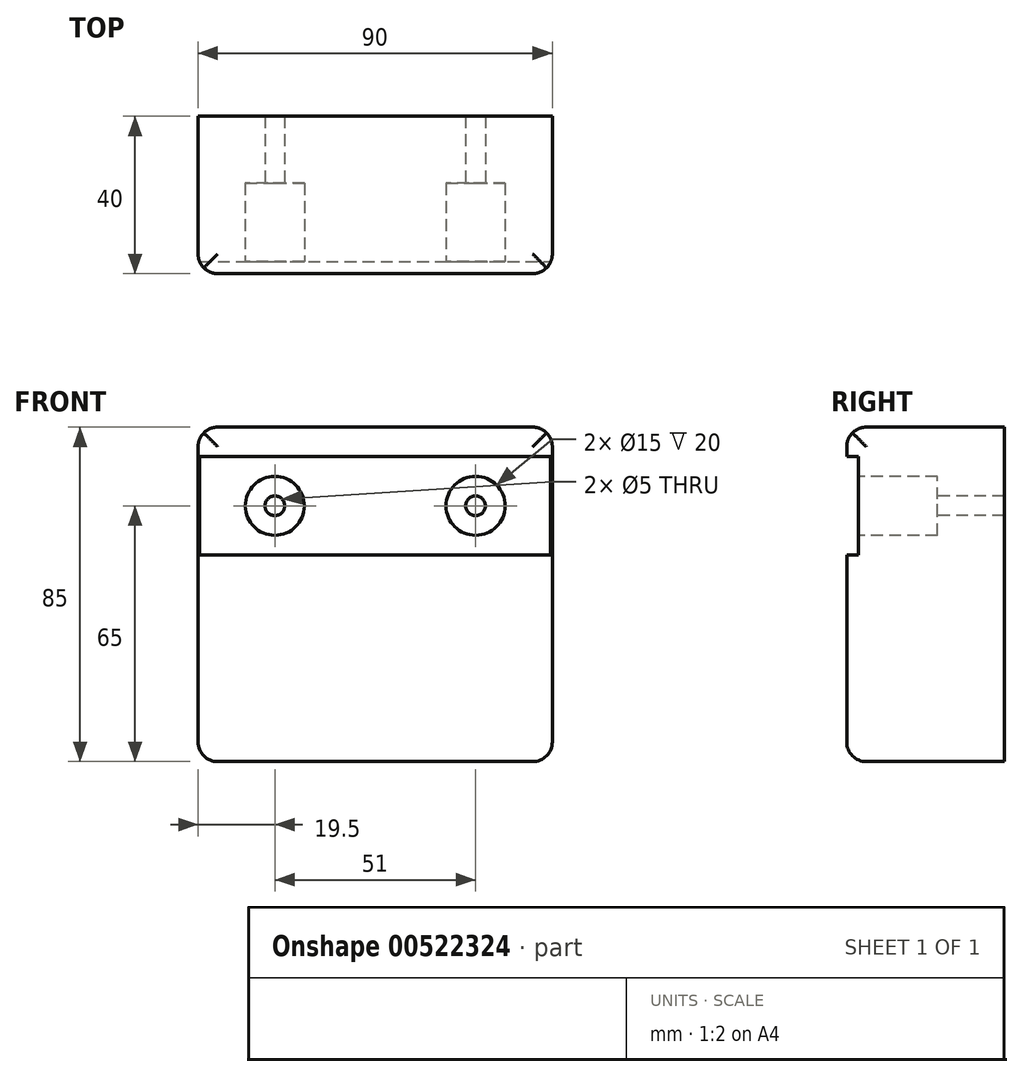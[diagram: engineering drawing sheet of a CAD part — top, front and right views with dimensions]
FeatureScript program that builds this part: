
annotation { "Feature Type Name" : "Feature", "Feature Type Description" : "" }
export const myFeature = defineFeature(function(context is Context, id is Id, definition is map)
    precondition{}
    {
        {
            var Q0;
            Q0=qCreatedBy(makeId("Front.planeOp"),FACE);
            var sketch = newSketch(context, id + "F0", { "sketchPlane" : qUnion([Q0])});
            skLineSegment(sketch, "E0.bottom", {"start": v(45, -42.5) * mm, "end": v(-45, -42.5) * mm});
            skLineSegment(sketch, "E0.top", {"start": v(45, 42.5) * mm, "end": v(-45, 42.5) * mm});
            skLineSegment(sketch, "E0.left", {"start": v(45, -42.5) * mm, "end": v(45, 42.5) * mm});
            skLineSegment(sketch, "E0.right", {"start": v(-45, -42.5) * mm, "end": v(-45, 42.5) * mm});
            skPoint(sketch, "E0.middle", {"position": v(0, 0) * mm});
            skLineSegment(sketch, "E1.bottom", {"start": v(35, 32.5) * mm, "end": v(-35, 32.5) * mm, "construction": true});
            skLineSegment(sketch, "E1.top", {"start": v(35, -32.5) * mm, "end": v(-35, -32.5) * mm, "construction": true});
            skLineSegment(sketch, "E1.left", {"start": v(35, 32.5) * mm, "end": v(35, -32.5) * mm, "construction": true});
            skLineSegment(sketch, "E1.right", {"start": v(-35, 32.5) * mm, "end": v(-35, -32.5) * mm, "construction": true});
            skSolve(sketch);
        }
        {
            var Q0;
            Q0 = qSketchRegion(id + "F0", true);
            extrude(context, id + "F1", {"entities" : qUnion([Q0]), "depth" : 40 * mm, "offsetDistance" : 25 * mm});
        }
        {
            var Q0;
            Q0=makeQuery(id+"F1.opExtrude","CAP_FACE",FACE,{"disambiguationData":[OSD([sQuery(id+"F0.wireOp",EDGE,"E0.bottom"),sQuery(id+"F0.wireOp",EDGE,"E0.top"),sQuery(id+"F0.wireOp",EDGE,"E0.left"),sQuery(id+"F0.wireOp",EDGE,"E0.right")])],"isStart":false});
            var sketch = newSketch(context, id + "F2", { "sketchPlane" : qUnion([Q0])});
            skLineSegment(sketch, "E2.bottom", {"start": v(-45, 10) * mm, "end": v(45, 10) * mm});
            skLineSegment(sketch, "E2.top", {"start": v(-45, 35) * mm, "end": v(45, 35) * mm});
            skLineSegment(sketch, "E2.left", {"start": v(-45, 10) * mm, "end": v(-45, 35) * mm});
            skLineSegment(sketch, "E2.right", {"start": v(45, 10) * mm, "end": v(45, 35) * mm});
            skLineSegment(sketch, "E3", {"start": v(-45, 22.5) * mm, "end": v(45, 22.5) * mm, "construction": true});
            skSolve(sketch);
        }
        {
            var Q0;
            Q0 = qSketchRegion(id + "F2", true);
            extrude(context, id + "F3", {"entities" : qUnion([Q0]), "operationType" : NewBodyOperationType.REMOVE, "oppositeDirection" : true, "depth" : 3 * mm, "offsetDistance" : 25 * mm});
        }
        {
            var Q0;
            Q0=makeQuery(id+"F3.boolean.opBoolean","COPY",FACE,{"derivedFrom":makeQuery(id+"F3.opExtrude","CAP_FACE",FACE,{"disambiguationData":[OSD([sQuery(id+"F2.wireOp",EDGE,"E2.bottom"),sQuery(id+"F2.wireOp",EDGE,"E2.top"),sQuery(id+"F2.wireOp",EDGE,"E2.left"),sQuery(id+"F2.wireOp",EDGE,"E2.right")])],"isStart":false})});
            var sketch = newSketch(context, id + "F4", { "sketchPlane" : qUnion([Q0])});
            skCircle(sketch, "E4", {"center": v(-25.5, 22.5) * mm, "radius": 7.5 * mm});
            skCircle(sketch, "E5", {"center": v(25.5, 22.5) * mm, "radius": 7.5 * mm});
            skLineSegment(sketch, "E6", {"start": v(-25.5, 22.5) * mm, "end": v(25.5, 22.5) * mm, "construction": true});
            skLineSegment(sketch, "E7", {"start": v(0, -42.5) * mm, "end": v(0, 42.5) * mm, "construction": true});
            skPoint(sketch, "E8", {"position": v(0, 22.5) * mm});
            skSolve(sketch);
        }
        {
            var Q0;
            Q0 = qSketchRegion(id + "F4", true);
            extrude(context, id + "F5", {"entities" : qUnion([Q0]), "operationType" : NewBodyOperationType.REMOVE, "oppositeDirection" : true, "depth" : 20 * mm, "offsetDistance" : 25 * mm});
        }
        {
            var Q0;
            Q0=makeQuery(id+"F3.boolean.opBoolean","COPY",FACE,{"derivedFrom":makeQuery(id+"F3.opExtrude","CAP_FACE",FACE,{"disambiguationData":[OSD([sQuery(id+"F2.wireOp",EDGE,"E2.bottom"),sQuery(id+"F2.wireOp",EDGE,"E2.top"),sQuery(id+"F2.wireOp",EDGE,"E2.left"),sQuery(id+"F2.wireOp",EDGE,"E2.right")])],"isStart":false})});
            var sketch = newSketch(context, id + "F6", { "sketchPlane" : qUnion([Q0])});
            skCircle(sketch, "E9", {"center": v(-25.5, 22.5) * mm, "radius": 2.5 * mm});
            skCircle(sketch, "E10", {"center": v(25.5, 22.5) * mm, "radius": 2.5 * mm});
            skSolve(sketch);
        }
        {
            var Q0;
            {var subQ0=sQuery(id+"F0.wireOp",EDGE,"E0.bottom");var subQ1=sQuery(id+"F0.wireOp",EDGE,"E0.left");Q0=makeQuery(id+"F3.boolean.opBoolean","SPLIT",EDGE,{"disambiguationData":[TD([makeQuery(id+"F1.opExtrude","SWEPT_FACE",FACE,{"disambiguationData":[OSD([subQ0])]})])],"derivedFrom":makeQuery(id+"F1.opExtrude","CAP_EDGE",EDGE,{"disambiguationData":[OSD([subQ1])],"isStart":false})});}
            var Q1;
            Q1=makeQuery(id+"F1.opExtrude","CAP_EDGE",EDGE,{"disambiguationData":[OSD([sQuery(id+"F0.wireOp",EDGE,"E0.bottom")])],"isStart":false});
            var Q2;
            {var subQ0=sQuery(id+"F0.wireOp",EDGE,"E0.bottom");var subQ1=sQuery(id+"F0.wireOp",EDGE,"E0.right");Q2=makeQuery(id+"F3.boolean.opBoolean","SPLIT",EDGE,{"disambiguationData":[TD([makeQuery(id+"F1.opExtrude","SWEPT_FACE",FACE,{"disambiguationData":[OSD([subQ0])]})])],"derivedFrom":makeQuery(id+"F1.opExtrude","CAP_EDGE",EDGE,{"disambiguationData":[OSD([subQ1])],"isStart":false})});}
            var Q3;
            Q3=makeQuery(id+"F1.opExtrude","CAP_EDGE",EDGE,{"disambiguationData":[OSD([sQuery(id+"F0.wireOp",EDGE,"E0.top")])],"isStart":false});
            var Q4;
            Q4=makeQuery(id+"F1.opExtrude","SWEPT_EDGE",EDGE,{"disambiguationData":[OSD([sQuery(id+"F0.wireOp",EDGE,"E0.top"),sQuery(id+"F0.wireOp",EDGE,"E0.right")])]});
            var Q5;
            Q5=makeQuery(id+"F1.opExtrude","SWEPT_EDGE",EDGE,{"disambiguationData":[OSD([sQuery(id+"F0.wireOp",EDGE,"E0.bottom"),sQuery(id+"F0.wireOp",EDGE,"E0.right")])]});
            var Q6;
            Q6=makeQuery(id+"F1.opExtrude","SWEPT_EDGE",EDGE,{"disambiguationData":[OSD([sQuery(id+"F0.wireOp",EDGE,"E0.bottom"),sQuery(id+"F0.wireOp",EDGE,"E0.left")])]});
            var Q7;
            Q7=makeQuery(id+"F1.opExtrude","SWEPT_EDGE",EDGE,{"disambiguationData":[OSD([sQuery(id+"F0.wireOp",EDGE,"E0.top"),sQuery(id+"F0.wireOp",EDGE,"E0.left")])]});
            fillet(context, id + "F7", {"entities" : qUnion([Q0, Q1, Q2, Q3, Q4, Q5, Q6, Q7]), "radius" : 5 * mm, "tangentPropagation" : true, "allowEdgeOverflow" : false});
        }
        {
            var Q0;
            Q0 = qSketchRegion(id + "F6", true);
            extrude(context, id + "F8", {"entities" : qUnion([Q0]), "operationType" : NewBodyOperationType.REMOVE, "endBound" : BoundingType.THROUGH_ALL, "oppositeDirection" : true, "depth" : 25 * mm, "offsetDistance" : 25 * mm});
        }
    });
